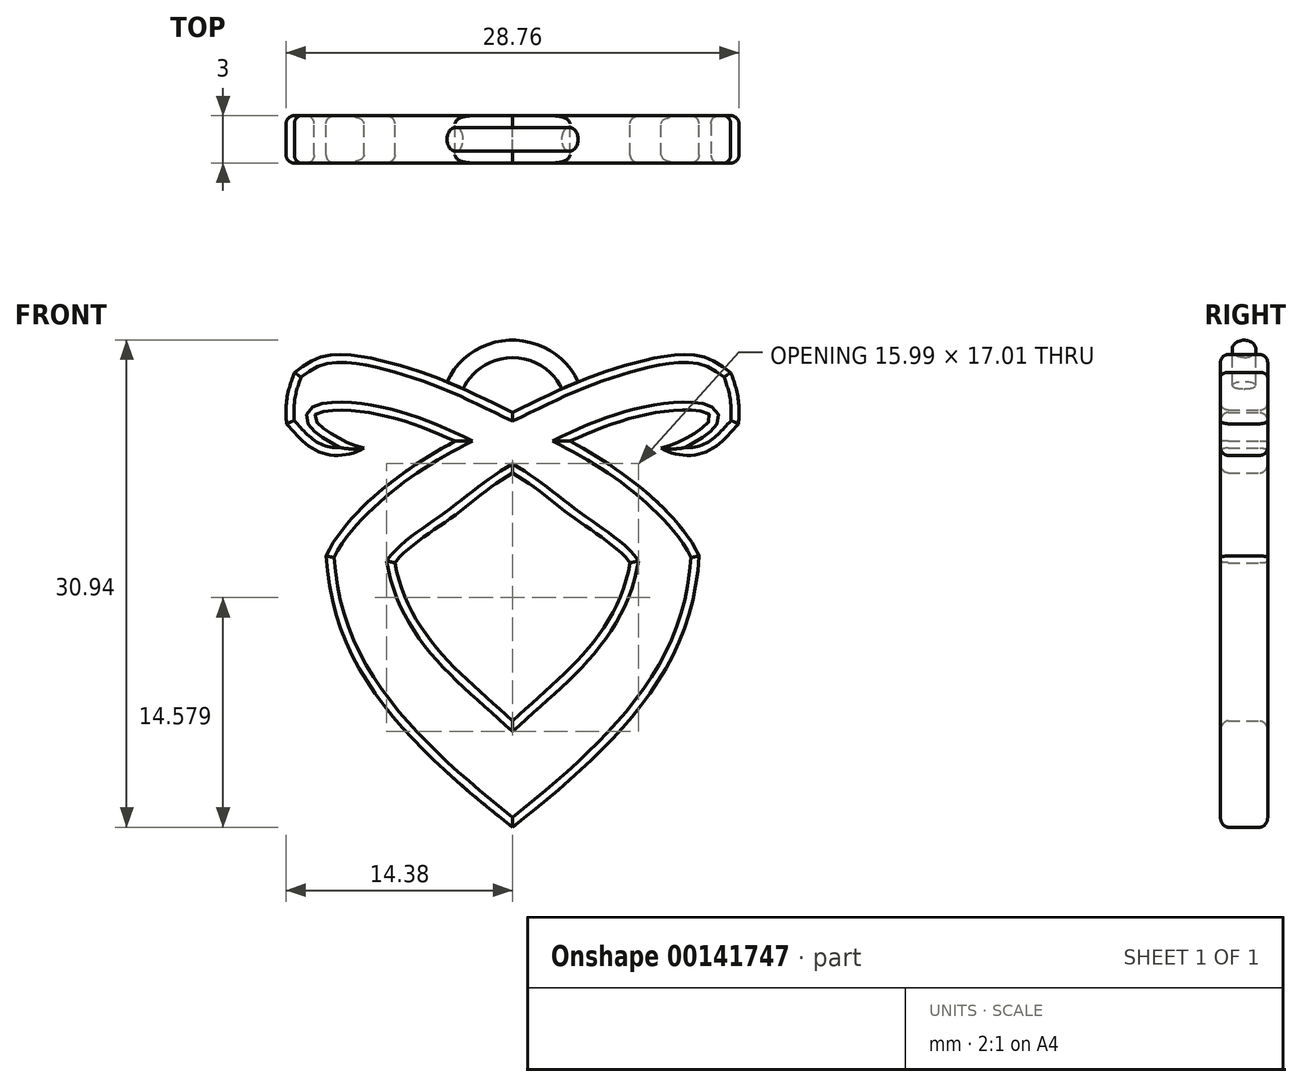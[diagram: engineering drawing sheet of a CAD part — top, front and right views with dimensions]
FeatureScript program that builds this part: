
annotation { "Feature Type Name" : "Feature", "Feature Type Description" : "" }
export const myFeature = defineFeature(function(context is Context, id is Id, definition is map)
    precondition{}
    {
        {
            var Q0;
            Q0=qCreatedBy(makeId("Front.planeOp"),FACE);
            var sketch = newSketch(context, id + "F0", { "sketchPlane" : qUnion([Q0])});
            skLineSegment(sketch, "E0", {"start": v(-33.36, 30) * mm, "end": v(35.98, 30) * mm, "construction": true});
            skFitSpline(sketch, "E1", {"points": [v(0, 26.34) * mm, v(-4.8, 28.54) * mm, v(-11.44, 30) * mm, v(-13.86, 28.9) * mm], "startDerivative": vector(-17.6, 8.33) * mm, "endDerivative": vector(-8.12, -5.96) * mm});
            skFitSpline(sketch, "E2", {"points": [v(-14.36, 25.62) * mm, v(-12.35, 23.86) * mm, v(-9.43, 24.09) * mm], "startDerivative": vector(3.08, -3.18) * mm, "endDerivative": vector(4.72, 3.1) * mm});
            skFitSpline(sketch, "E3", {"points": [v(-9.43, 24.09) * mm, v(-11.4, 24.92) * mm, v(-12.6, 26.08) * mm, v(-9.43, 26.38) * mm, v(0, 22.5) * mm], "startDerivative": vector(-9.43, 1.64) * mm, "endDerivative": vector(23.9, -14.9) * mm});
            skLineSegment(sketch, "E4", {"start": v(-3.65, 24.51) * mm, "end": v(-3.65, 24.51) * mm});
            skFitSpline(sketch, "E5", {"points": [v(-11.84, 17.23) * mm, v(-8.68, 8.43) * mm, v(0, 0) * mm], "startDerivative": vector(1.3, -21.8) * mm, "endDerivative": vector(19.26, -15.1) * mm});
            skLineSegment(sketch, "E6", {"start": v(0, 22.5) * mm, "end": v(0, 22.5) * mm});
            skFitSpline(sketch, "E7", {"points": [v(-7.47, 16.8) * mm, v(-4.4, 10.89) * mm, v(0, 6.75) * mm], "startDerivative": vector(2.35, -13.8) * mm, "endDerivative": vector(8.25, -7.62) * mm});
            skFitSpline(sketch, "E8", {"points": [v(-13.86, 28.9) * mm, v(-14.32, 27.3) * mm, v(-14.36, 25.62) * mm], "startDerivative": vector(-1.13, -3.15) * mm, "endDerivative": vector(0.12, -3.39) * mm});
            skFitSpline(sketch, "E9.MirrorCS", {"points": [v(0, 26.34) * mm, v(4.8, 28.54) * mm, v(11.44, 30) * mm, v(13.86, 28.9) * mm], "startDerivative": vector(17.6, 8.33) * mm, "endDerivative": vector(8.12, -5.96) * mm});
            skFitSpline(sketch, "E10.MirrorCS", {"points": [v(13.86, 28.9) * mm, v(14.32, 27.3) * mm, v(14.36, 25.62) * mm], "startDerivative": vector(1.13, -3.15) * mm, "endDerivative": vector(-0.12, -3.39) * mm});
            skFitSpline(sketch, "E11.MirrorCS", {"points": [v(14.36, 25.62) * mm, v(12.35, 23.86) * mm, v(9.43, 24.09) * mm], "startDerivative": vector(-3.08, -3.18) * mm, "endDerivative": vector(-4.72, 3.1) * mm});
            skFitSpline(sketch, "E12.MirrorCS", {"points": [v(9.43, 24.09) * mm, v(11.4, 24.92) * mm, v(12.6, 26.08) * mm, v(9.43, 26.38) * mm, v(0, 22.5) * mm], "startDerivative": vector(9.43, 1.64) * mm, "endDerivative": vector(-23.9, -14.9) * mm});
            skFitSpline(sketch, "E13.MirrorCS", {"points": [v(0, 26.34) * mm, v(6.11, 23.06) * mm, v(11.84, 17.23) * mm], "startDerivative": vector(12.81, -6.45) * mm, "endDerivative": vector(5.85, -12.57) * mm});
            skFitSpline(sketch, "E14.MirrorCS", {"points": [v(11.84, 17.23) * mm, v(8.68, 8.43) * mm, v(0, 0) * mm], "startDerivative": vector(-1.3, -21.8) * mm, "endDerivative": vector(-19.26, -15.1) * mm});
            skFitSpline(sketch, "E15.MirrorCS", {"points": [v(7.47, 16.8) * mm, v(4.4, 10.89) * mm, v(0, 6.75) * mm], "startDerivative": vector(-2.35, -13.8) * mm, "endDerivative": vector(-8.25, -7.62) * mm});
            skFitSpline(sketch, "E16.MirrorCS", {"points": [v(0, 22.5) * mm, v(3.66, 19.83) * mm, v(7.47, 16.8) * mm], "startDerivative": vector(10.28, -6.12) * mm, "endDerivative": vector(3.25, -4.98) * mm});
            skLineSegment(sketch, "E17", {"start": v(3.65, 24.51) * mm, "end": v(3.65, 24.51) * mm});
            skFitSpline(sketch, "E18", {"points": [v(0, 26.34) * mm, v(-6.11, 23.06) * mm, v(-11.84, 17.23) * mm], "startDerivative": vector(-12.81, -6.45) * mm, "endDerivative": vector(-5.85, -12.57) * mm});
            skFitSpline(sketch, "E19", {"points": [v(0, 22.5) * mm, v(-3.66, 19.83) * mm, v(-7.47, 16.8) * mm], "startDerivative": vector(-10.28, -6.12) * mm, "endDerivative": vector(-3.25, -4.98) * mm});
            skSolve(sketch);
        }
        {
            var Q0;
            Q0 = qSketchRegion(id + "F0", true);
            extrude(context, id + "F1", {"entities" : qUnion([Q0]), "depth" : 3 * mm});
        }
        {
            var Q0;
            Q0=makeQuery(id+"F1.opExtrude","CAP_EDGE",EDGE,{"disambiguationData":[OSD([sQuery(id+"F0.wireOp",EDGE,"E18")])],"isStart":false});
            var Q1;
            Q1=makeQuery(id+"F1.opExtrude","CAP_EDGE",EDGE,{"disambiguationData":[OSD([sQuery(id+"F0.wireOp",EDGE,"E5")])],"isStart":false});
            var Q2;
            Q2=makeQuery(id+"F1.opExtrude","CAP_EDGE",EDGE,{"disambiguationData":[OSD([sQuery(id+"F0.wireOp",EDGE,"E14.MirrorCS")])],"isStart":false});
            var Q3;
            Q3=makeQuery(id+"F1.opExtrude","CAP_EDGE",EDGE,{"disambiguationData":[OSD([sQuery(id+"F0.wireOp",EDGE,"E13.MirrorCS")])],"isStart":false});
            var Q4;
            Q4=makeQuery(id+"F1.opExtrude","CAP_EDGE",EDGE,{"disambiguationData":[OSD([sQuery(id+"F0.wireOp",EDGE,"E1")])],"isStart":false});
            var Q5;
            Q5=makeQuery(id+"F1.opExtrude","CAP_EDGE",EDGE,{"disambiguationData":[OSD([sQuery(id+"F0.wireOp",EDGE,"E8")])],"isStart":false});
            var Q6;
            Q6=makeQuery(id+"F1.opExtrude","CAP_EDGE",EDGE,{"disambiguationData":[OSD([sQuery(id+"F0.wireOp",EDGE,"E2")])],"isStart":false});
            var Q7;
            Q7=makeQuery(id+"F1.opExtrude","CAP_EDGE",EDGE,{"disambiguationData":[OSD([sQuery(id+"F0.wireOp",EDGE,"E3")])],"isStart":false});
            var Q8;
            Q8=makeQuery(id+"F1.opExtrude","CAP_EDGE",EDGE,{"disambiguationData":[OSD([sQuery(id+"F0.wireOp",EDGE,"E12.MirrorCS")])],"isStart":false});
            var Q9;
            Q9=makeQuery(id+"F1.opExtrude","CAP_EDGE",EDGE,{"disambiguationData":[OSD([sQuery(id+"F0.wireOp",EDGE,"E11.MirrorCS")])],"isStart":false});
            var Q10;
            Q10=makeQuery(id+"F1.opExtrude","CAP_EDGE",EDGE,{"disambiguationData":[OSD([sQuery(id+"F0.wireOp",EDGE,"E10.MirrorCS")])],"isStart":false});
            var Q11;
            Q11=makeQuery(id+"F1.opExtrude","CAP_FACE",FACE,{"disambiguationData":[OSD([sQuery(id+"F0.wireOp",EDGE,"E1"),sQuery(id+"F0.wireOp",EDGE,"E2"),sQuery(id+"F0.wireOp",EDGE,"E3"),sQuery(id+"F0.wireOp",EDGE,"E5"),sQuery(id+"F0.wireOp",EDGE,"E7"),sQuery(id+"F0.wireOp",EDGE,"E8"),sQuery(id+"F0.wireOp",EDGE,"E9.MirrorCS"),sQuery(id+"F0.wireOp",EDGE,"E10.MirrorCS"),sQuery(id+"F0.wireOp",EDGE,"E11.MirrorCS"),sQuery(id+"F0.wireOp",EDGE,"E12.MirrorCS"),sQuery(id+"F0.wireOp",EDGE,"E13.MirrorCS"),sQuery(id+"F0.wireOp",EDGE,"E14.MirrorCS"),sQuery(id+"F0.wireOp",EDGE,"E15.MirrorCS"),sQuery(id+"F0.wireOp",EDGE,"E16.MirrorCS"),sQuery(id+"F0.wireOp",EDGE,"E18"),sQuery(id+"F0.wireOp",EDGE,"E19")])],"isStart":false});
            var Q12;
            Q12=makeQuery(id+"F1.opExtrude","CAP_EDGE",EDGE,{"disambiguationData":[OSD([sQuery(id+"F0.wireOp",EDGE,"E10.MirrorCS")])],"isStart":true});
            var Q13;
            Q13=makeQuery(id+"F1.opExtrude","CAP_EDGE",EDGE,{"disambiguationData":[OSD([sQuery(id+"F0.wireOp",EDGE,"E9.MirrorCS")])],"isStart":true});
            var Q14;
            Q14=makeQuery(id+"F1.opExtrude","CAP_EDGE",EDGE,{"disambiguationData":[OSD([sQuery(id+"F0.wireOp",EDGE,"E1")])],"isStart":true});
            var Q15;
            Q15=makeQuery(id+"F1.opExtrude","CAP_EDGE",EDGE,{"disambiguationData":[OSD([sQuery(id+"F0.wireOp",EDGE,"E8")])],"isStart":true});
            var Q16;
            Q16=makeQuery(id+"F1.opExtrude","CAP_EDGE",EDGE,{"disambiguationData":[OSD([sQuery(id+"F0.wireOp",EDGE,"E2")])],"isStart":true});
            var Q17;
            Q17=makeQuery(id+"F1.opExtrude","CAP_EDGE",EDGE,{"disambiguationData":[OSD([sQuery(id+"F0.wireOp",EDGE,"E3")])],"isStart":true});
            var Q18;
            Q18=makeQuery(id+"F1.opExtrude","CAP_EDGE",EDGE,{"disambiguationData":[OSD([sQuery(id+"F0.wireOp",EDGE,"E18")])],"isStart":true});
            var Q19;
            Q19=makeQuery(id+"F1.opExtrude","CAP_EDGE",EDGE,{"disambiguationData":[OSD([sQuery(id+"F0.wireOp",EDGE,"E5")])],"isStart":true});
            var Q20;
            Q20=makeQuery(id+"F1.opExtrude","CAP_EDGE",EDGE,{"disambiguationData":[OSD([sQuery(id+"F0.wireOp",EDGE,"E14.MirrorCS")])],"isStart":true});
            var Q21;
            Q21=makeQuery(id+"F1.opExtrude","CAP_EDGE",EDGE,{"disambiguationData":[OSD([sQuery(id+"F0.wireOp",EDGE,"E13.MirrorCS")])],"isStart":true});
            var Q22;
            Q22=makeQuery(id+"F1.opExtrude","CAP_EDGE",EDGE,{"disambiguationData":[OSD([sQuery(id+"F0.wireOp",EDGE,"E12.MirrorCS")])],"isStart":true});
            var Q23;
            Q23=makeQuery(id+"F1.opExtrude","CAP_EDGE",EDGE,{"disambiguationData":[OSD([sQuery(id+"F0.wireOp",EDGE,"E11.MirrorCS")])],"isStart":true});
            var Q24;
            Q24=makeQuery(id+"F1.opExtrude","CAP_EDGE",EDGE,{"disambiguationData":[OSD([sQuery(id+"F0.wireOp",EDGE,"E10.MirrorCS")])],"isStart":true});
            var Q25;
            Q25=makeQuery(id+"F1.opExtrude","CAP_EDGE",EDGE,{"disambiguationData":[OSD([sQuery(id+"F0.wireOp",EDGE,"E16.MirrorCS")])],"isStart":true});
            var Q26;
            Q26=makeQuery(id+"F1.opExtrude","CAP_EDGE",EDGE,{"disambiguationData":[OSD([sQuery(id+"F0.wireOp",EDGE,"E19")])],"isStart":true});
            var Q27;
            Q27=makeQuery(id+"F1.opExtrude","CAP_EDGE",EDGE,{"disambiguationData":[OSD([sQuery(id+"F0.wireOp",EDGE,"E7")])],"isStart":true});
            var Q28;
            Q28=makeQuery(id+"F1.opExtrude","CAP_EDGE",EDGE,{"disambiguationData":[OSD([sQuery(id+"F0.wireOp",EDGE,"E15.MirrorCS")])],"isStart":true});
            fillet(context, id + "F2", {"entities" : qUnion([Q0, Q1, Q2, Q3, Q4, Q5, Q6, Q7, Q8, Q9, Q10, Q11, Q12, Q13, Q14, Q15, Q16, Q17, Q18, Q19, Q20, Q21, Q22, Q23, Q24, Q25, Q26, Q27, Q28]), "radius" : 0.5 * mm, "tangentPropagation" : true, "allowEdgeOverflow" : false});
        }
        {
            var Q0;
            Q0=qCreatedBy(makeId("Top.planeOp"),FACE);
            cPlane(context, id + "F3", {"entities" : qUnion([Q0]), "cplaneType" : CPlaneType.OFFSET, "offset" : 29 * mm, "width" : 150 * mm, "height" : 150 * mm});
        }
        {
            var Q0;
            Q0=qCreatedBy(id+"F3.planeOp",FACE);
            var sketch = newSketch(context, id + "F4", { "sketchPlane" : qUnion([Q0])});
            skCircle(sketch, "E20", {"center": v(-3, -1.5) * mm, "radius": 0.75 * mm});
            skSolve(sketch);
        }
        {
            var Q0;
            Q0 = qSketchRegion(id + "F4", true);
            var Q1;
            Q1=makeQuery(id+"F1.opExtrude","SWEPT_EDGE",EDGE,{"disambiguationData":[OSD([sQuery(id+"F0.wireOp",EDGE,"E1"),sQuery(id+"F0.wireOp",EDGE,"E9.MirrorCS")])]});
            revolve(context, id + "F5", {"operationType" : NewBodyOperationType.ADD, "entities" : qUnion([Q0]), "axis" : qUnion([Q1]), "revolveType" : RevolveType.TWO_DIRECTIONS, "angle" : 150 * degree, "angleBack" : 330 * degree});
        }
    });
